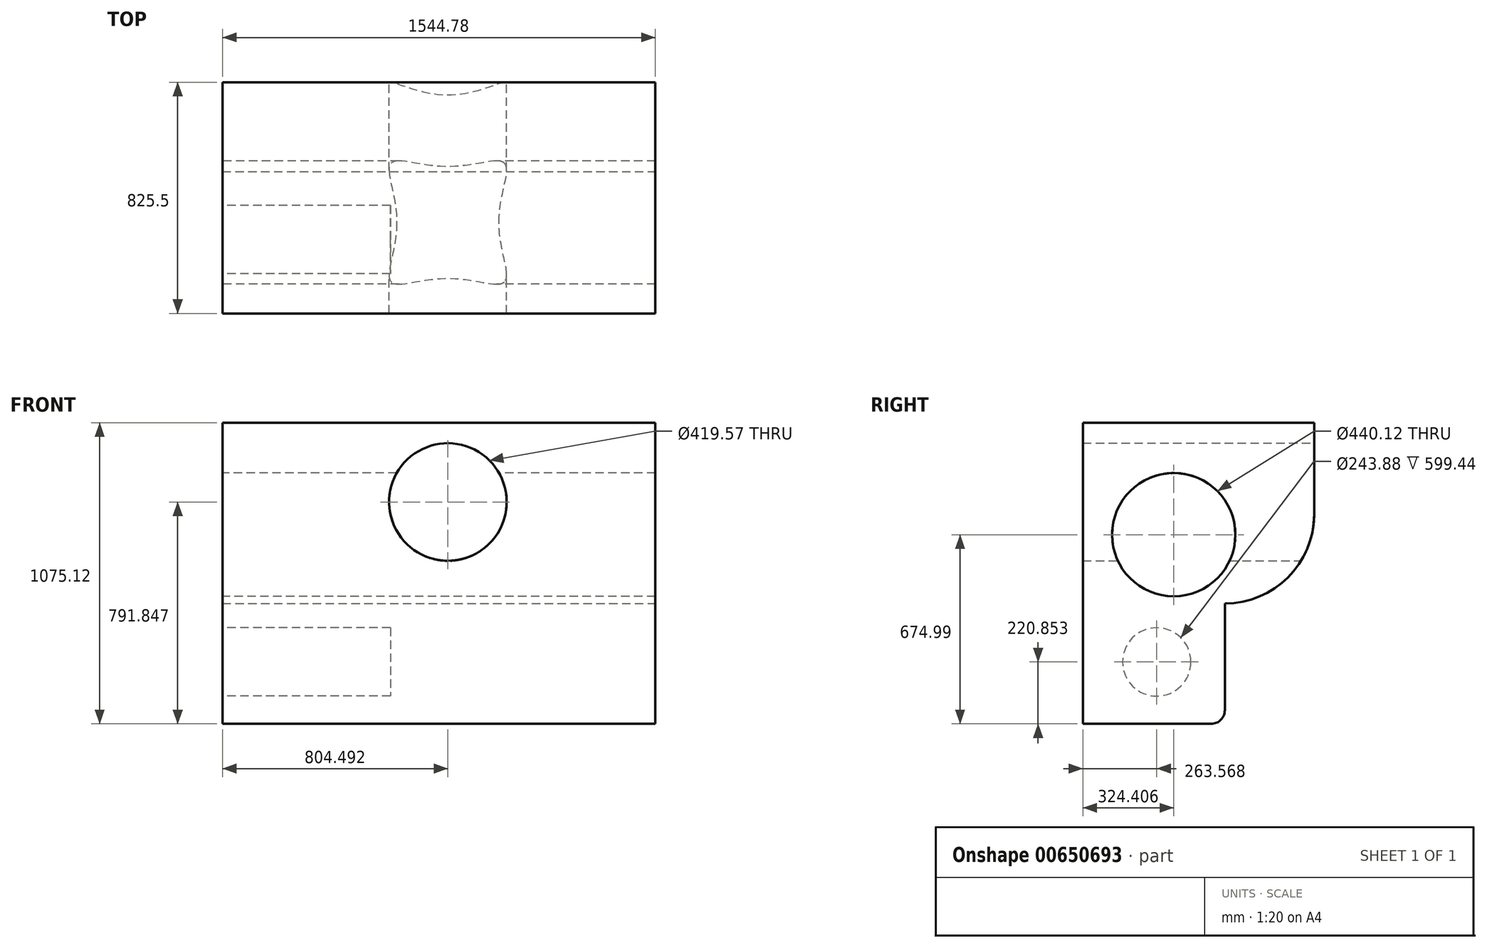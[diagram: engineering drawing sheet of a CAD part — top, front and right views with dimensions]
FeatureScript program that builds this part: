
annotation { "Feature Type Name" : "Feature", "Feature Type Description" : "" }
export const myFeature = defineFeature(function(context is Context, id is Id, definition is map)
    precondition{}
    {
        {
            var Q0;
            Q0=qCreatedBy(makeId("Front.planeOp"),FACE);
            var sketch = newSketch(context, id + "F0", { "sketchPlane" : qUnion([Q0])});
            skLineSegment(sketch, "E0.bottom", {"start": v(-844.15, -296.5) * mm, "end": v(700.63, -296.5) * mm});
            skLineSegment(sketch, "E0.top", {"start": v(-844.15, 349.37) * mm, "end": v(700.63, 349.37) * mm});
            skLineSegment(sketch, "E0.left", {"start": v(-844.15, -296.5) * mm, "end": v(-844.15, 349.37) * mm});
            skLineSegment(sketch, "E0.right", {"start": v(700.63, -296.5) * mm, "end": v(700.63, 349.37) * mm});
            skCircle(sketch, "E1", {"center": v(-39.66, 66.1) * mm, "radius": 209.78 * mm});
            skSolve(sketch);
        }
        {
            var Q0;
            Q0=makeQuery(id+"F0.imprint","IMPRINT",FACE,{"disambiguationData":[TD([[makeQuery(id+"F0.imprint","IMPRINT",EDGE,{"derivedFrom":sQuery(id+"F0.wireOp",EDGE,"E0.bottom")}),1.0]])]});
            extrude(context, id + "F1", {"entities" : qUnion([Q0]), "depth" : 825.5 * mm, "offsetDistance" : 25.4 * mm});
        }
        {
            var Q0;
            Q0=makeQuery(id+"F1.opExtrude","CAP_EDGE",EDGE,{"disambiguationData":[OSD([sQuery(id+"F0.wireOp",EDGE,"E0.bottom")])],"isStart":true});
            fillet(context, id + "F2", {"entities" : qUnion([Q0]), "radius" : 318.87 * mm, "tangentPropagation" : true, "allowEdgeOverflow" : false});
        }
        {
            var Q0;
            Q0=makeQuery(id+"F1.opExtrude","SWEPT_FACE",FACE,{"disambiguationData":[OSD([sQuery(id+"F0.wireOp",EDGE,"E0.bottom")])]});
            extrude(context, id + "F3", {"entities" : qUnion([Q0]), "operationType" : NewBodyOperationType.ADD, "depth" : 429.26 * mm, "offsetDistance" : 25.4 * mm});
        }
        {
            var Q0;
            {var subQ0=sQuery(id+"F0.wireOp",EDGE,"E0.left");Q0=makeQuery(id+"F3.boolean.opBoolean","MERGE",FACE,{"derivedFrom":[makeQuery(id+"F1.opExtrude","SWEPT_FACE",FACE,{"disambiguationData":[OSD([subQ0])]}),makeQuery(id+"F3.opExtrude","SWEPT_FACE",FACE,{"disambiguationData":[OSD([sQuery(id+"F0.wireOp",EDGE,"E0.bottom"),subQ0])]})]});}
            var sketch = newSketch(context, id + "F4", { "sketchPlane" : qUnion([Q0])});
            skCircle(sketch, "E2", {"center": v(501.1, -50.76) * mm, "radius": 220.06 * mm});
            skCircle(sketch, "E3", {"center": v(561.93, -504.9) * mm, "radius": 121.94 * mm});
            skSolve(sketch);
        }
        {
            var Q0;
            Q0=makeQuery(id+"F4.imprint","IMPRINT",FACE,{"disambiguationData":[TD([[makeQuery(id+"F4.imprint","IMPRINT",EDGE,{"derivedFrom":sQuery(id+"F4.wireOp",EDGE,"E2")}),1.0]])]});
            extrude(context, id + "F5", {"entities" : qUnion([Q0]), "operationType" : NewBodyOperationType.REMOVE, "oppositeDirection" : true, "depth" : 1765.3 * mm, "offsetDistance" : 25.4 * mm});
        }
        {
            var Q0;
            {var subQ0=sQuery(id+"F0.wireOp",EDGE,"E0.bottom");Q0=makeQuery(id+"F3.opExtrude","CAP_EDGE",EDGE,{"disambiguationData":[OSD([subQ0]),TDD([makeQuery(id+"F2.opFillet","BLEND_EDGE",EDGE,{"blendedFrom":[makeQuery(id+"F1.opExtrude","CAP_EDGE",EDGE,{"disambiguationData":[OSD([subQ0])],"isStart":true}),makeQuery(id+"F1.opExtrude","SWEPT_FACE",FACE,{"disambiguationData":[OSD([subQ0])]})],"blendedInto":[makeQuery(id+"F1.opExtrude","SWEPT_FACE",FACE,{"disambiguationData":[OSD([subQ0])]})]})])],"isStart":false});}
            fillet(context, id + "F6", {"entities" : qUnion([Q0]), "radius" : 48.26 * mm, "tangentPropagation" : true, "allowEdgeOverflow" : false});
        }
        {
            var Q0;
            Q0=makeQuery(id+"F4.imprint","IMPRINT",FACE,{"disambiguationData":[TD([[makeQuery(id+"F4.imprint","IMPRINT",EDGE,{"derivedFrom":sQuery(id+"F4.wireOp",EDGE,"E3")}),1.0]])]});
            extrude(context, id + "F7", {"entities" : qUnion([Q0]), "operationType" : NewBodyOperationType.REMOVE, "oppositeDirection" : true, "depth" : 599.44 * mm, "offsetDistance" : 25.4 * mm});
        }
    });
